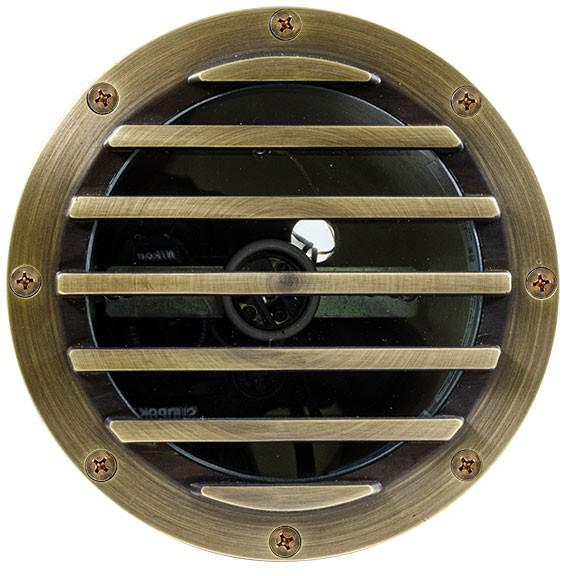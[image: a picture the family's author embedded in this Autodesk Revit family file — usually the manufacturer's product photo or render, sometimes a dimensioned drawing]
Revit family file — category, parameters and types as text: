
# Revit family: Alcon-9150-Q360-Revit-Family
name_source: partatom
category: Luminarias
units: mm (PartAtom-declared; Revit-internal decimal feet)

## family parameters
Anfitrión = Cara
Compartido = No
Corte con vacíos al cargar = No
Cota de conector redondo = Usar diámetro
Mantener orientación de anotación = No
Origen de luz = Sí
Punto de cálculo de habitación = No
Tipo de pieza = Normal

## types (1)
- Alcon-9150-Q360-Revit-Family
    Cambio de temperatura de color de luz atenuada = <Ninguno>
    Elevación por defecto = 4' - 0"
    Fabricante = Alcon Lighting
    Filtro de color = 16777215
    GLASS LENS = Analytical Panels
    HOUSING = <Por categoría>
    LENS GLASS = Glass
    Link to IES File = https://www.alconlighting.com
    Longitud de símbolo de origen de luz = 10' - 0"
    Modelo = Alcon Lighting 9150-Q360
    Product Data URL = https://www.alconlighting.com
    Product Page = https://www.alconlighting.com
    TAP LENS = <Por categoría>
    TOP FINISH = <Por categoría>
    URL = https://www.alconlighting.com
    Ángulo de campo de foco = 90.00°
    Ángulo de enfoque = 30.00°
    Ángulo de inclinación = 60.00°

## geometry (parser evidence)
native form markers: Sweep x3
no freeform markers — native parametric forms only
